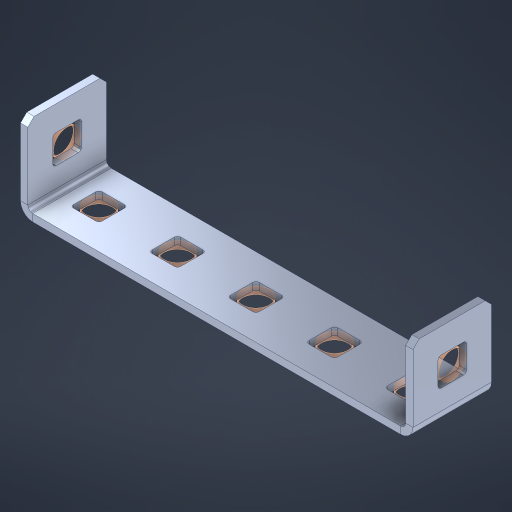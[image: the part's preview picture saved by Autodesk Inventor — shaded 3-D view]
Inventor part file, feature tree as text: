
AUTODESK INVENTOR PART (.ipt)
format: ipt  version: 2023 (Build 270158000, 158)  size: 452,096 bytes
history: native  units: in
note: dims shown in document units (in); Inventor stores cm internally (conversion verified against a paired STEP export)
features: other x12, sheet_metal_op x10, sketch x8, extrude x6, mirror x1, pattern_linear x1, chamfer x1
ambient origin geometry x8: Origin, YZ Plane, XZ Plane, XY Plane, X Axis, Y Axis, Z Axis, Center Point
bodies: Solid1 (feature_tree), Body (feature_tree)
feature tree (39):
  other  "Flange Pattern Plane"
  sheet_metal_op  "Flange Pattern"
  sheet_metal_op  "Body Pattern"
  other  "Arc Length"
  mirror  "Notch Mirror"
  pattern_linear  "Notch Pattern"  Spacing1=0.1875in  [1 undecoded]
  chamfer  "End Chamfer"
  extrude  "Half Cut"  Depth=0.0469in
  sketch  "Sketch1"  dims[d0=2.5in]
  other  "Plate1"
  sketch  "Sketch2"  dims[d1=0.5in]
  other  "Plate2"
  sheet_metal_op  "Bend1"
  sheet_metal_op  "Corner1"
  sketch  "Sketch3"  dims[d2=0.0469in]
  other  "Flange Pattern Sketch"
  sketch  "Sketch7"  dims[d3=0.0469in]
  other  "Srf1"
  other  "Srf2"
  sketch  "Sketch8"  dims[d4=0.0234in]
  sketch  "Sketch9"  dims[d5=0.0938in]
  other  "Srf91"
  sheet_metal_op  "Body Pattern Sketch"
  other  "Srf92"
  sketch  "Sketch13"  dims[d6=0.0469in]
  sketch  "Sketch14"  dims[d7=0.5in d8=90.0deg d9=0.0312in d10=0.1875in d11=0.0469in d12=0.0469in d16=0.182in d17=0.02in d18=0.0469in d19=0.0in d20=0.25in d21=0.25in d46=0.172in d47=1.0in d48=0.0in d49=0.182in d50=0.02in d51=0.25in d52=0.25in d53=0.0469in d54=0.0in d55=0.172in d56=1.0in d57=0.0in d60=0.3937in d62=0.5in d63=1.9685in d65=0.5in d85=0.1227in d86=0.1659in d88=0.04in d89=0.0469in d90=0.0in d91=0.04in d92=0.0491in d95=2.5in d96=0.04in d97=0.25in d98=45.0deg d101=0.0in d102=2.497in d131=2.5in d132=0.3937in d134=0.5in]
  other  "Srf856"
  other  "Srf1376"
  other  "Srf1377"
  sheet_metal_op  "Flange Stamp"
  sheet_metal_op  "Flange Circle"
  sheet_metal_op  "Body Stamp"
  sheet_metal_op  "Body Circle"
  sheet_metal_op  "Notch"
  extrude  "ExtrusionSrf2"  Depth=0.0469in
  extrude  "ExtrusionSrf92"  Depth=0.182in
  extrude  "ExtrusionSrf856"  Depth=0.02in
  extrude  "ExtrusionSrf1376"  Depth=0.0469in
  extrude  "ExtrusionSrf1377"  TaperAngle=0.0deg  [1 undecoded]
note: 2 required parameter values undecoded (feature->parameter linkage not recoverable at this tier; creation-order binding heuristic only, values carry confidence <= 0.55)
